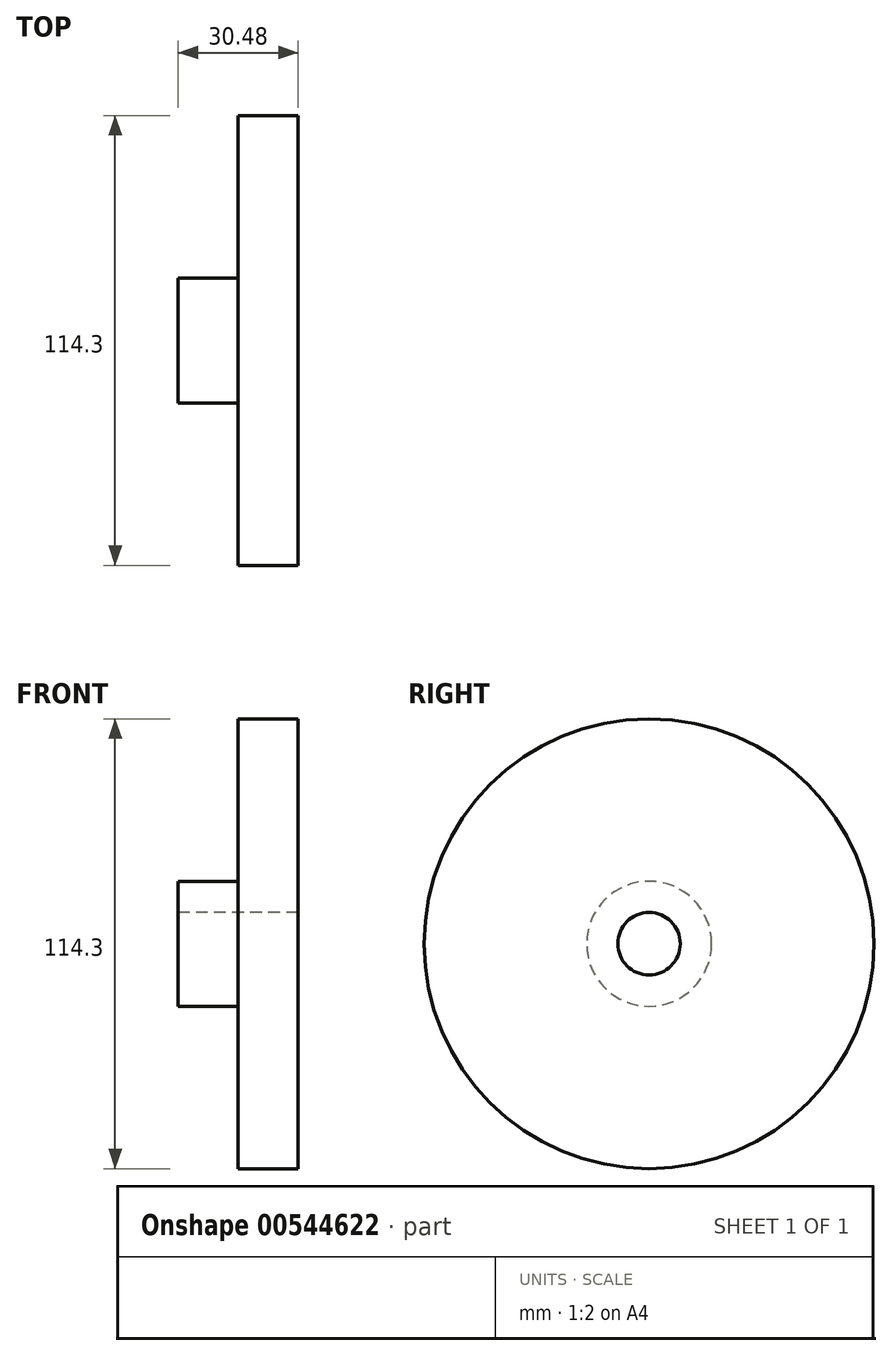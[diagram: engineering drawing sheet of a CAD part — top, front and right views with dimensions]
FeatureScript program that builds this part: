
annotation { "Feature Type Name" : "Feature", "Feature Type Description" : "" }
export const myFeature = defineFeature(function(context is Context, id is Id, definition is map)
    precondition{}
    {
        {
            var Q0;
            Q0=qCreatedBy(makeId("Front.planeOp"),FACE);
            var sketch = newSketch(context, id + "F0", { "sketchPlane" : qUnion([Q0])});
            skLineSegment(sketch, "E0", {"start": v(0, 7.94) * mm, "end": v(0, 15.88) * mm});
            skLineSegment(sketch, "E1", {"start": v(0, 15.88) * mm, "end": v(15.24, 15.88) * mm});
            skLineSegment(sketch, "E2", {"start": v(15.24, 15.88) * mm, "end": v(15.24, 57.15) * mm});
            skLineSegment(sketch, "E3", {"start": v(15.24, 57.15) * mm, "end": v(30.48, 57.15) * mm});
            skLineSegment(sketch, "E4", {"start": v(0, 0) * mm, "end": v(81.3, 0) * mm, "construction": true});
            skLineSegment(sketch, "E5", {"start": v(0, 7.94) * mm, "end": v(30.48, 7.94) * mm});
            skLineSegment(sketch, "E6", {"start": v(30.48, 57.15) * mm, "end": v(30.48, 7.94) * mm});
            skSolve(sketch);
        }
        {
            var Q0;
            Q0=makeQuery(id+"F0.imprint","IMPRINT",FACE,{"disambiguationData":[TD([[makeQuery(id+"F0.imprint","IMPRINT",EDGE,{"derivedFrom":sQuery(id+"F0.wireOp",EDGE,"E0")}),-1.0]])]});
            var Q1;
            Q1=sQuery(id+"F0.wireOp",EDGE,"E4");
            revolve(context, id + "F1", {"surfaceOperationType" : NewSurfaceOperationType.NEW, "entities" : qUnion([Q0]), "axis" : qUnion([Q1]), "revolveType" : RevolveType.FULL});
        }
    });
